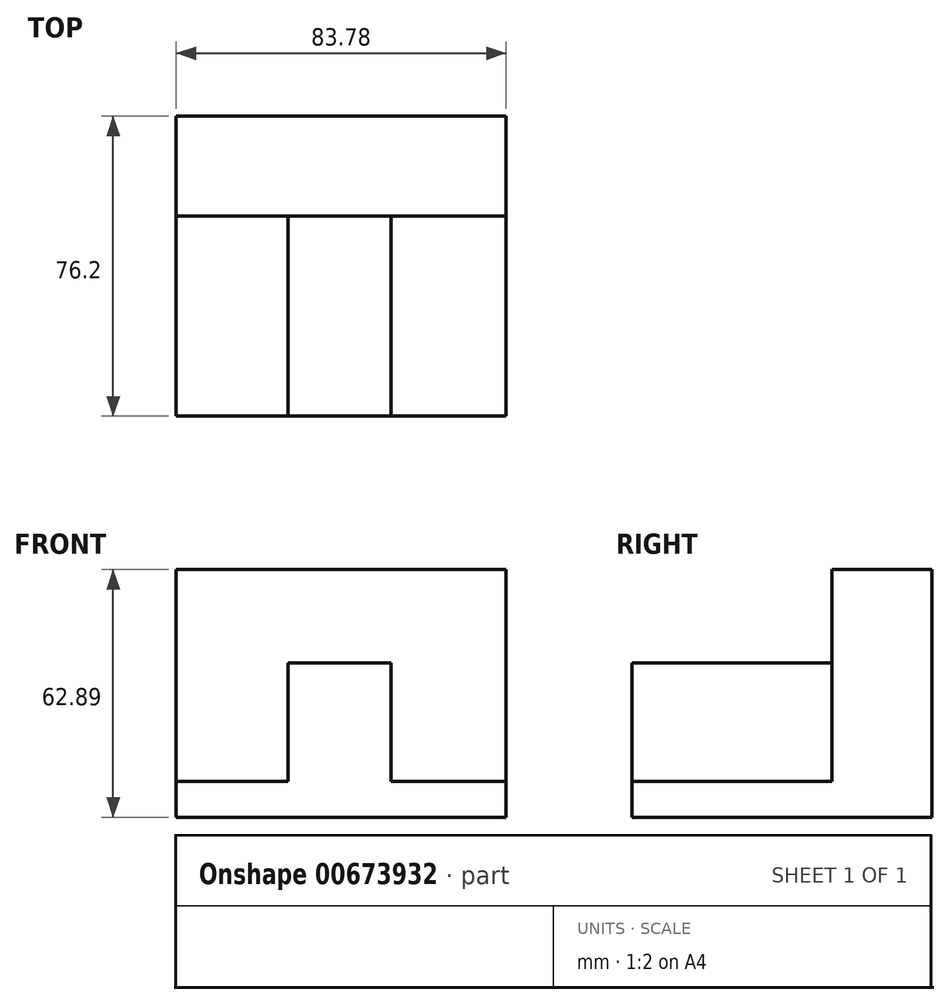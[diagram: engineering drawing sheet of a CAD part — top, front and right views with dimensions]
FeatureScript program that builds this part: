
annotation { "Feature Type Name" : "Feature", "Feature Type Description" : "" }
export const myFeature = defineFeature(function(context is Context, id is Id, definition is map)
    precondition{}
    {
        {
            var Q0;
            Q0=qCreatedBy(makeId("Front.planeOp"),FACE);
            var sketch = newSketch(context, id + "F0", { "sketchPlane" : qUnion([Q0])});
            skLineSegment(sketch, "E0.bottom", {"start": v(41.9, 30.11) * mm, "end": v(-41.9, 30.11) * mm});
            skLineSegment(sketch, "E0.top", {"start": v(41.9, -32.78) * mm, "end": v(-41.9, -32.78) * mm});
            skLineSegment(sketch, "E0.left", {"start": v(41.9, 30.11) * mm, "end": v(41.9, -32.78) * mm});
            skLineSegment(sketch, "E0.right", {"start": v(-41.9, 30.11) * mm, "end": v(-41.9, -32.78) * mm});
            skSolve(sketch);
        }
        {
            var Q0;
            Q0=makeQuery(id+"F0.imprint","IMPRINT",FACE,{"disambiguationData":[TD([[makeQuery(id+"F0.imprint","IMPRINT",EDGE,{"derivedFrom":sQuery(id+"F0.wireOp",EDGE,"E0.bottom")}),1.0]])]});
            extrude(context, id + "F1", {"entities" : qUnion([Q0]), "oppositeDirection" : true, "depth" : 25.4 * mm, "offsetDistance" : 25.4 * mm});
        }
        {
            var Q0;
            Q0=makeQuery(id+"F1.opExtrude","CAP_FACE",FACE,{"disambiguationData":[OSD([sQuery(id+"F0.wireOp",EDGE,"E0.bottom"),sQuery(id+"F0.wireOp",EDGE,"E0.top"),sQuery(id+"F0.wireOp",EDGE,"E0.left"),sQuery(id+"F0.wireOp",EDGE,"E0.right")])],"isStart":true});
            var sketch = newSketch(context, id + "F2", { "sketchPlane" : qUnion([Q0])});
            skLineSegment(sketch, "E1", {"start": v(-41.9, -23.62) * mm, "end": v(-13.48, -23.62) * mm});
            skLineSegment(sketch, "E2", {"start": v(-13.48, -23.62) * mm, "end": v(-13.48, 6.44) * mm});
            skLineSegment(sketch, "E3", {"start": v(-13.48, 6.44) * mm, "end": v(12.68, 6.44) * mm});
            skLineSegment(sketch, "E4", {"start": v(12.68, 6.44) * mm, "end": v(12.68, -23.62) * mm});
            skLineSegment(sketch, "E5", {"start": v(12.68, -23.62) * mm, "end": v(41.9, -23.62) * mm});
            skSolve(sketch);
        }
        {
            var Q0;
            {var subQ0=sQuery(id+"F2.wireOp",EDGE,"E1");Q0=makeQuery(id+"F2.imprint","IMPRINT",FACE,{"disambiguationData":[TD([[makeQuery(id+"F2.imprint","IMPRINT",EDGE,{"derivedFrom":subQ0}),-1.0]])]});}
            extrude(context, id + "F3", {"entities" : qUnion([Q0]), "operationType" : NewBodyOperationType.ADD, "depth" : 50.8 * mm, "offsetDistance" : 25.4 * mm});
        }
    });
